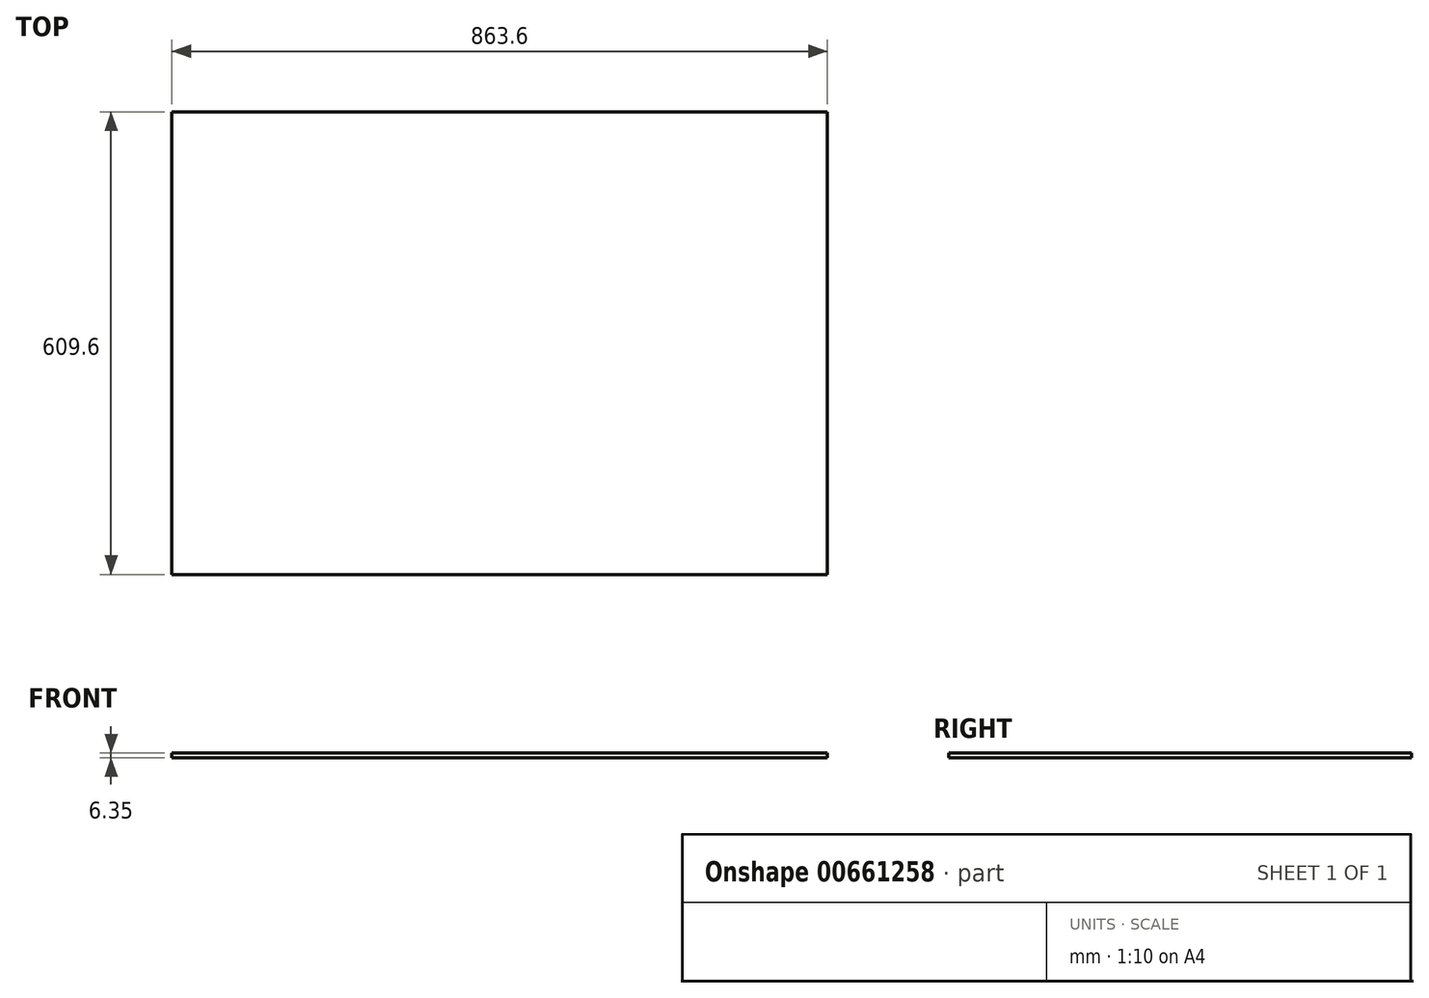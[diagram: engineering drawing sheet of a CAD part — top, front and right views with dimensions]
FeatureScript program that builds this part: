
annotation { "Feature Type Name" : "Feature", "Feature Type Description" : "" }
export const myFeature = defineFeature(function(context is Context, id is Id, definition is map)
    precondition{}
    {
        {
            var Q0;
            Q0=qCreatedBy(makeId("Top.planeOp"),FACE);
            var sketch = newSketch(context, id + "F0", { "sketchPlane" : qUnion([Q0])});
            skLineSegment(sketch, "E0.bottom", {"start": v(-798.46, 553.26) * mm, "end": v(65.14, 553.26) * mm});
            skLineSegment(sketch, "E0.top", {"start": v(-798.46, -56.34) * mm, "end": v(65.14, -56.34) * mm});
            skLineSegment(sketch, "E0.left", {"start": v(-798.46, 553.26) * mm, "end": v(-798.46, -56.34) * mm});
            skLineSegment(sketch, "E0.right", {"start": v(65.14, 553.26) * mm, "end": v(65.14, -56.34) * mm});
            skSolve(sketch);
        }
        {
            var Q0;
            Q0=makeQuery(id+"F0.imprint","IMPRINT",FACE,{"disambiguationData":[TD([[makeQuery(id+"F0.imprint","IMPRINT",EDGE,{"derivedFrom":sQuery(id+"F0.wireOp",EDGE,"E0.bottom")}),-1.0]])]});
            extrude(context, id + "F1", {"entities" : qUnion([Q0]), "depth" : 6.35 * mm, "offsetDistance" : 25.4 * mm});
        }
    });
